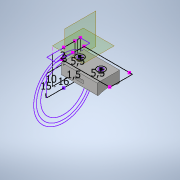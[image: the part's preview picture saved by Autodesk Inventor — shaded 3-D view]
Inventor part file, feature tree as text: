
AUTODESK INVENTOR PART (.ipt)
format: ipt  version: 2021.1 (Build 251245010, 245A)  size: 236,544 bytes
history: native  units: in
note: dims shown in document units (in); Inventor stores cm internally (conversion verified against a paired STEP export)
features: extrude x11, sketch x5, plane x2, fillet x1
ambient origin geometry x8: Origin, YZ Plane, XZ Plane, XY Plane, X Axis, Y Axis, Z Axis, Center Point
bodies: Solid1 (feature_tree)
feature tree (19):
  plane  "Arbeitsebene1"
  sketch  "Skizze1"  dims[d0=0.2165in d1=0.2165in]
  extrude  "Extrusion1"  Depth=0.2165in
  plane  "Arbeitsebene2"
  sketch  "Skizze2"  dims[d2=0.3937in d3=0.0in d4=0.5906in]
  extrude  "Extrusion2"  Depth=0.3937in
  extrude  "Extrusion3"  Depth=0.3937in
  extrude  "Extrusion4"  Depth=0.3937in TaperAngle=0.0deg
  extrude  "Extrusion5"  Depth=0.0197in
  extrude  "Extrusion6"  Depth=0.0197in
  extrude  "Extrusion7"  Depth=0.0197in TaperAngle=0.0deg
  extrude  "Extrusion8"  Depth=0.0197in TaperAngle=0.0deg
  extrude  "Extrusion9"  Depth=0.0197in TaperAngle=0.0deg
  fillet  "Rundung1"  Radius=0.6516in
  extrude  "Extrusion10"  Depth=0.0197in TaperAngle=0.0deg
  extrude  "Extrusion11"  Depth=0.0197in TaperAngle=0.0deg
  sketch  "Skizze4"  dims[d5=0.6299in d6=0.3937in]
  sketch  "Skizze6"  dims[d7=0.0591in d8=0.3937in d9=0.0in]
  sketch  "Skizze7"  dims[d12=0.1969in d13=0.0in d14=0.1181in d15=0.0787in d16=1.4961in d17=0.0in d18=1.2795in d19=0.0in d20=0.8681in d21=0.0in d22=0.6516in d23=0.0in d24=0.6516in d25=0.0in d26=0.0787in d27=0.0in d28=0.0197in d29=0.2205in d30=0.2205in d31=0.3543in d32=0.0in d33=0.2598in d34=0.0in]
